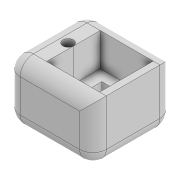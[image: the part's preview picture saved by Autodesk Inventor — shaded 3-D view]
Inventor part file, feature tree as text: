
AUTODESK INVENTOR PART (.ipt)
format: ipt  version: 2022 (Build 260153000, 153)  size: 160,256 bytes
history: native  units: mm
features: extrude x4, sketch x4, fillet x1, projected_geometry x1
ambient origin geometry x8: Origin, YZ Plane, XZ Plane, XY Plane, X Axis, Y Axis, Z Axis, Center Point
bodies: Solid1 (feature_tree)
feature tree (10):
  extrude  "Extrusion1"  Depth=8.0mm
  extrude  "Extrusion2"  Depth=2.0mm
  extrude  "Extrusion3"  Depth=4.0mm
  extrude  "Extrusion4"  Depth=4.0mm TaperAngle=0.0deg
  fillet  "Fillet1"  Radius=1.6mm
  sketch  "Sketch1"  dims[d0=8.1mm d1=8.0mm]
  sketch  "Sketch2"  dims[d5=2.0mm d6=2.0mm]
  projected_geometry  "Projected Loop1"
  sketch  "Sketch3"  dims[d7=1.0mm d8=4.0mm]
  sketch  "Sketch4"  dims[d9=5.0mm d10=0.0mm d11=4.0mm d12=0.0mm d14=1.6mm d15=100.0mm d16=0.0mm d17=5.0mm d18=3.8mm d19=2.0mm d20=100.0mm d21=0.0mm d22=2.0mm]
